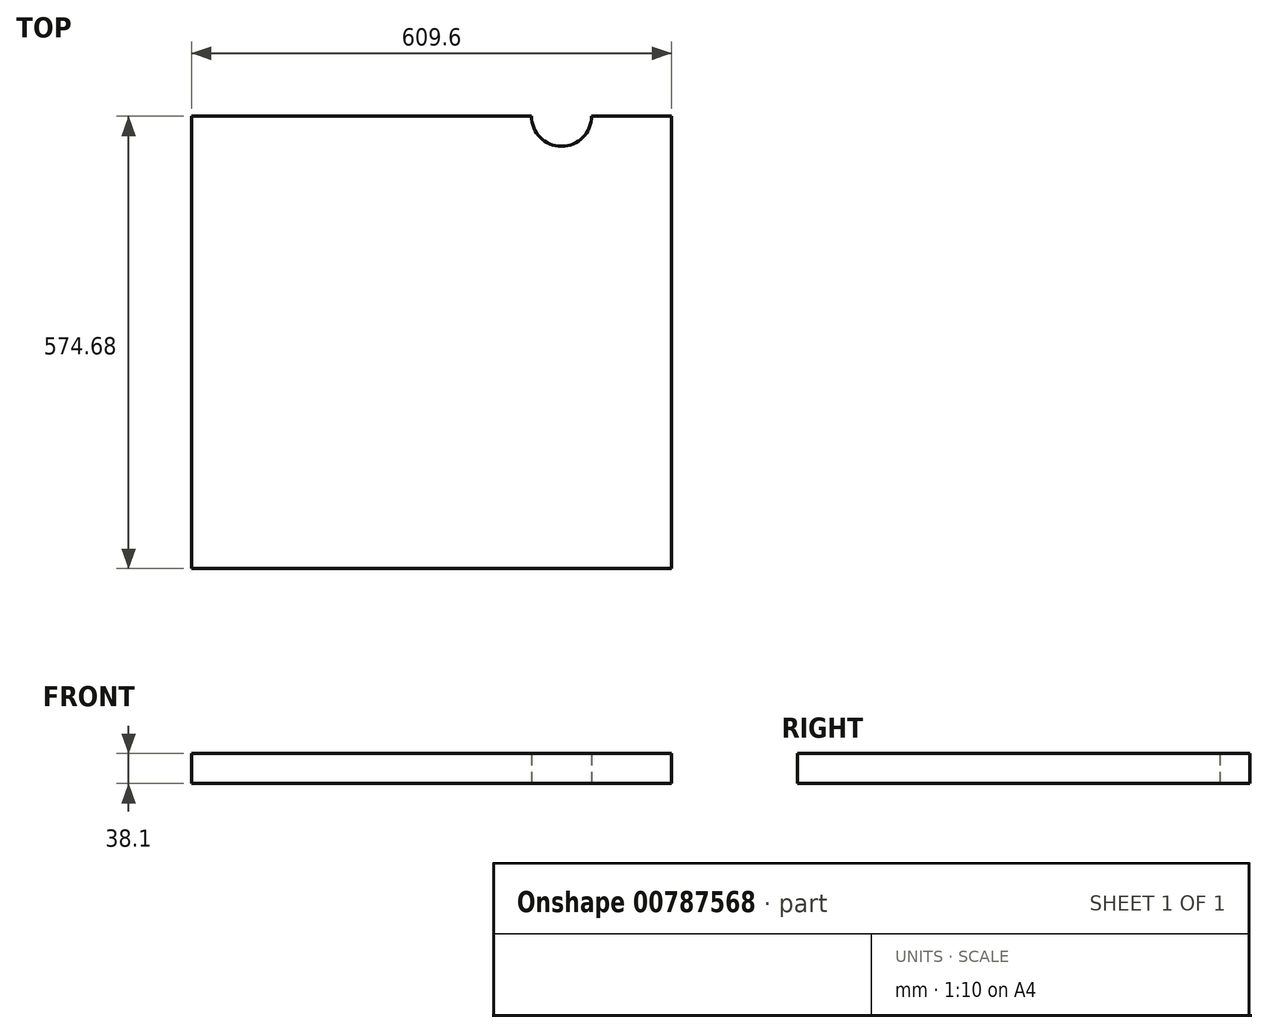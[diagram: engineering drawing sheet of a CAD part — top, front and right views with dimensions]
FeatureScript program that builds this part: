
annotation { "Feature Type Name" : "Feature", "Feature Type Description" : "" }
export const myFeature = defineFeature(function(context is Context, id is Id, definition is map)
    precondition{}
    {
        {
            var Q0;
            Q0=qCreatedBy(makeId("Top.planeOp"),FACE);
            var sketch = newSketch(context, id + "F0", { "sketchPlane" : qUnion([Q0])});
            skLineSegment(sketch, "E0.bottom", {"start": v(304.8, 287.34) * mm, "end": v(-304.8, 287.34) * mm});
            skLineSegment(sketch, "E0.top", {"start": v(304.8, -287.34) * mm, "end": v(-304.8, -287.34) * mm});
            skLineSegment(sketch, "E0.left", {"start": v(304.8, 287.34) * mm, "end": v(304.8, -287.34) * mm});
            skLineSegment(sketch, "E0.right", {"start": v(-304.8, 287.34) * mm, "end": v(-304.8, -287.34) * mm});
            skPoint(sketch, "E0.middle", {"position": v(0, 0) * mm});
            skArc(sketch, "E1", {"start": v(127, 287.34) * mm, "mid": v(165.1, 249.24) * mm, "end": v(203.2, 287.34) * mm});
            skSolve(sketch);
        }
        {
            var Q0;
            Q0=qSketchRegion(id+"F0",true);
            extrude(context, id + "F1", {"entities" : qUnion([Q0]), "depth" : 38.1 * mm, "offsetDistance" : 25.4 * mm});
        }
        {
            var Q0;
            {var subQ0=sQuery(id+"F0.wireOp",EDGE,"E1");Q0=makeQuery(id+"F0.imprint","IMPRINT",FACE,{"disambiguationData":[TD([[makeQuery(id+"F0.imprint","IMPRINT",EDGE,{"derivedFrom":subQ0}),1.0]])]});}
            extrude(context, id + "F2", {"entities" : qUnion([Q0]), "operationType" : NewBodyOperationType.REMOVE, "depth" : 38.1 * mm, "offsetDistance" : 25.4 * mm});
        }
    });
